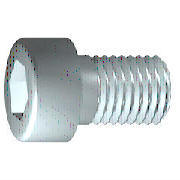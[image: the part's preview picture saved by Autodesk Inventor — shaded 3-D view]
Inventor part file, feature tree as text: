
AUTODESK INVENTOR PART (.ipt)
format: ipt  version: 2020 (Build 240168000, 168)  size: 187,392 bytes
history: native  units: mm (DEFAULTED — no unit token found)
features: sketch x2, other x1, extrude x1, plane x1, fillet x1
ambient origin geometry x7: Origin, YZ Plane, XY Plane, X Axis, Y Axis, Z Axis, Center Point
bodies: Solid1 (feature_tree)
feature tree (6):
  other  "Körper"
  extrude  "Loch"  Depth=4.0mm
  plane  "Work Plane1"
  fillet  "Fillet2"  Radius=4.0mm
  sketch  "Skizze1"  dims[d1=20.0mm d2=0.429515mm d3=4.0mm]
  sketch  "Skizze2"  dims[d4=2.0mm d5=60.0deg d6=4.0mm d7=4.0mm d8=3.464102mm d9=7.0mm d10=90.0deg d11=10.0mm d12=0.0mm d13=20.0mm d14=0.0mm d15=0.429415mm d16=0.429415mm d17=0.4mm d19=0.0mm d26=40.0mm d27=45.0deg d28=0.0mm d29=0.0mm d30=0.1mm]
